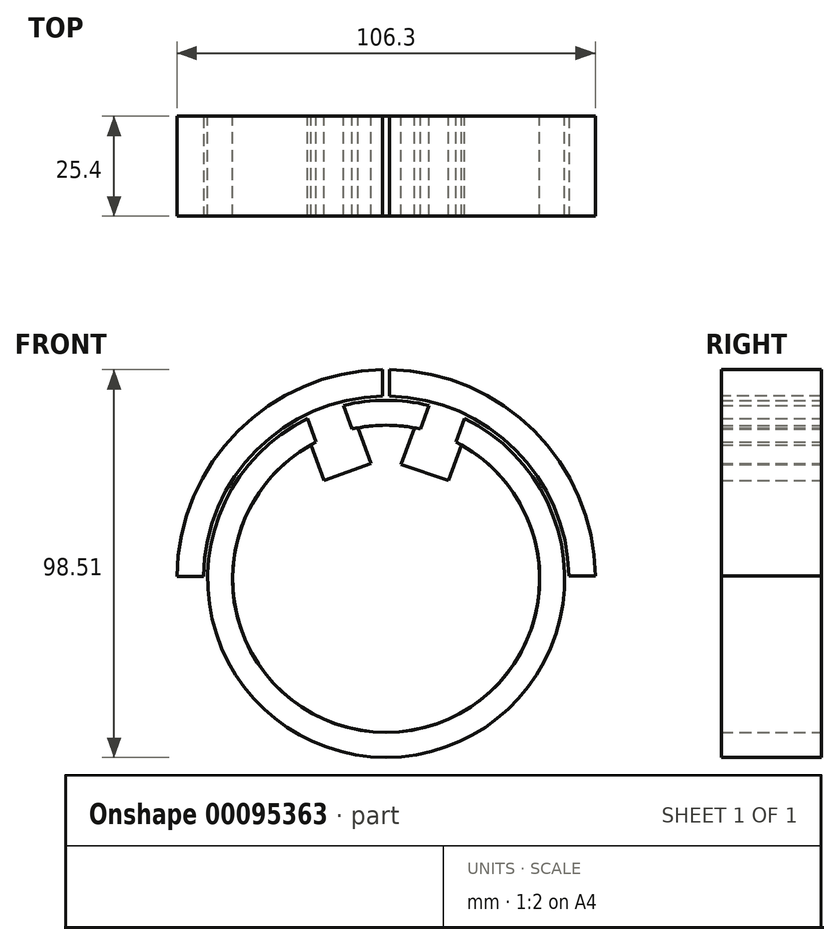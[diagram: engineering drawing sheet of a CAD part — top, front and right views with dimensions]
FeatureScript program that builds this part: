
annotation { "Feature Type Name" : "Feature", "Feature Type Description" : "" }
export const myFeature = defineFeature(function(context is Context, id is Id, definition is map)
    precondition{}
    {
        {
            var Q0;
            Q0=qCreatedBy(makeId("Front.planeOp"),FACE);
            var sketch = newSketch(context, id + "F0", { "sketchPlane" : qUnion([Q0])});
            skArc(sketch, "E0", {"start": v(-19.96, 40.74) * mm, "mid": v(0, -45.36) * mm, "end": v(19.96, 40.74) * mm});
            skArc(sketch, "E1", {"start": v(-17.78, 34.73) * mm, "mid": v(0, -39.02) * mm, "end": v(17.78, 34.73) * mm});
            skLineSegment(sketch, "E2", {"start": v(0, 77.3) * mm, "end": v(0, -77.42) * mm, "construction": true});
            skLineSegment(sketch, "E3", {"start": v(-103.05, 0) * mm, "end": v(124.24, 0) * mm, "construction": true});
            skLineSegment(sketch, "E4", {"start": v(0, 0) * mm, "end": v(-22.26, 61.17) * mm, "construction": true});
            skLineSegment(sketch, "E5", {"start": v(0, 0) * mm, "end": v(-64.24, 23.38) * mm, "construction": true});
            skLineSegment(sketch, "E6", {"start": v(-19.13, 34) * mm, "end": v(-15.83, 24.93) * mm});
            skLineSegment(sketch, "E7", {"start": v(-15.83, 24.93) * mm, "end": v(-3.9, 29.28) * mm});
            skLineSegment(sketch, "E8", {"start": v(-3.9, 29.28) * mm, "end": v(-7.2, 38.35) * mm});
            skLineSegment(sketch, "E9", {"start": v(0, 0) * mm, "end": v(24.43, 67.1) * mm, "construction": true});
            skLineSegment(sketch, "E10", {"start": v(17.7, 34.52) * mm, "end": v(19.13, 34) * mm});
            skLineSegment(sketch, "E11", {"start": v(7.2, 38.35) * mm, "end": v(3.84, 29.1) * mm});
            skLineSegment(sketch, "E12", {"start": v(3.84, 29.1) * mm, "end": v(15.83, 24.93) * mm});
            skLineSegment(sketch, "E13", {"start": v(15.83, 24.93) * mm, "end": v(19.13, 34) * mm});
            skLineSegment(sketch, "E14", {"start": v(-17.78, 34.73) * mm, "end": v(-19.96, 40.74) * mm});
            skLineSegment(sketch, "E15", {"start": v(-8.7, 38.03) * mm, "end": v(-10.9, 44.04) * mm});
            skLineSegment(sketch, "E16", {"start": v(8.7, 38.03) * mm, "end": v(10.9, 44.04) * mm});
            skLineSegment(sketch, "E17", {"start": v(17.7, 34.52) * mm, "end": v(19.96, 40.74) * mm});
            skArc(sketch, "E18.trimOffspring", {"start": v(10.9, 44.04) * mm, "mid": v(0, 45.36) * mm, "end": v(-10.9, 44.04) * mm});
            skArc(sketch, "E19.trimOffspring", {"start": v(8.7, 38.03) * mm, "mid": v(0, 39.02) * mm, "end": v(-8.7, 38.03) * mm});
            skSolve(sketch);
        }
        {
            var Q0;
            {var subQ3=sQuery(id+"F0.wireOp",EDGE,"E15");Q0=makeQuery(id+"F0.imprint","IMPRINT",FACE,{"disambiguationData":[TD([[makeQuery(id+"F0.imprint","IMPRINT",EDGE,{"derivedFrom":subQ3}),-1.0]])]});}
            var Q1;
            {var subQ6=sQuery(id+"F0.wireOp",EDGE,"E0");Q1=makeQuery(id+"F0.imprint","IMPRINT",FACE,{"disambiguationData":[TD([[makeQuery(id+"F0.imprint","IMPRINT",EDGE,{"derivedFrom":subQ6}),1.0]])]});}
            extrude(context, id + "F1", {"entities" : qUnion([Q0, Q1]), "depth" : 25.4 * mm});
        }
        {
            var Q0;
            {var subQ1=sQuery(id+"F0.wireOp",EDGE,"E6");Q0=makeQuery(id+"F0.imprint","IMPRINT",FACE,{"disambiguationData":[TD([[makeQuery(id+"F0.imprint","IMPRINT",EDGE,{"derivedFrom":subQ1}),-1.0]])]});}
            var sketch = newSketch(context, id + "F2", { "sketchPlane" : qUnion([Q0])});
            skSolve(sketch);
        }
        {
            var Q0;
            {var subQ1=sQuery(id+"F0.wireOp",EDGE,"E6");Q0=makeQuery(id+"F2.imprint","IMPRINT",FACE,{"disambiguationData":[TD([[makeQuery(id+"F2.imprint","IMPRINT",EDGE,{"derivedFrom":makeQuery(id+"F0.imprint","IMPRINT",EDGE,{"derivedFrom":subQ1})}),-1.0]])]});}
            extrude(context, id + "F3", {"entities" : qUnion([Q0]), "depth" : 25.4 * mm});
        }
        {
            var Q0;
            Q0=makeQuery(id+"F3.opExtrude","CAP_FACE",FACE,{"disambiguationData":[OSD([sQuery(id+"F0.wireOp",EDGE,"E1"),sQuery(id+"F0.wireOp",EDGE,"E6"),sQuery(id+"F0.wireOp",EDGE,"E7"),sQuery(id+"F0.wireOp",EDGE,"E8"),sQuery(id+"F0.wireOp",EDGE,"E11"),sQuery(id+"F0.wireOp",EDGE,"E12"),sQuery(id+"F0.wireOp",EDGE,"E13"),sQuery(id+"F0.wireOp",EDGE,"E19.trimOffspring")])],"isStart":false});
            var sketch = newSketch(context, id + "F4", { "sketchPlane" : qUnion([Q0])});
            skArc(sketch, "E20", {"start": v(-0.88, 46.41) * mm, "mid": v(-32.9, 32.75) * mm, "end": v(-46.42, 0.66) * mm});
            skArc(sketch, "E21", {"start": v(-0.88, 53.15) * mm, "mid": v(-37.67, 37.51) * mm, "end": v(-53.15, 0.66) * mm});
            skLineSegment(sketch, "E22", {"start": v(-0.88, 53.15) * mm, "end": v(-0.88, 46.41) * mm});
            skLineSegment(sketch, "E23", {"start": v(0.86, 53.15) * mm, "end": v(0.86, 46.41) * mm});
            skLineSegment(sketch, "E24", {"start": v(-53.15, 0.66) * mm, "end": v(-46.42, 0.66) * mm});
            skLineSegment(sketch, "E25", {"start": v(-53.15, -0.69) * mm, "end": v(-46.41, -0.69) * mm});
            skArc(sketch, "E26.trimOffspring", {"start": v(-53.15, -0.69) * mm, "mid": v(-0.07, -53.16) * mm, "end": v(53.15, -0.83) * mm});
            skArc(sketch, "E27.trimOffspring", {"start": v(-46.41, -0.69) * mm, "mid": v(-0.07, -46.42) * mm, "end": v(46.41, -0.83) * mm});
            skLineSegment(sketch, "E28", {"start": v(46.37, 0.7) * mm, "end": v(53.15, 0.7) * mm});
            skLineSegment(sketch, "E29", {"start": v(46.41, -0.83) * mm, "end": v(53.15, -0.83) * mm});
            skArc(sketch, "E30.trimOffspring", {"start": v(46.41, 0.7) * mm, "mid": v(32.88, 32.77) * mm, "end": v(0.86, 46.41) * mm});
            skArc(sketch, "E31.trimOffspring", {"start": v(53.15, 0.7) * mm, "mid": v(37.64, 37.53) * mm, "end": v(0.86, 53.15) * mm});
            skSolve(sketch);
        }
        {
            var Q0;
            Q0=makeQuery(id+"F4.imprint","IMPRINT",FACE,{"disambiguationData":[TD([[makeQuery(id+"F4.imprint","IMPRINT",EDGE,{"derivedFrom":sQuery(id+"F4.wireOp",EDGE,"E20")}),-1.0]])]});
            extrude(context, id + "F5", {"entities" : qUnion([Q0]), "oppositeDirection" : true, "depth" : 25.4 * mm});
        }
        {
            var Q0;
            Q0=makeQuery(id+"F4.imprint","IMPRINT",FACE,{"disambiguationData":[TD([[makeQuery(id+"F4.imprint","IMPRINT",EDGE,{"derivedFrom":sQuery(id+"F4.wireOp",EDGE,"E23")}),1.0]])]});
            extrude(context, id + "F6", {"entities" : qUnion([Q0]), "oppositeDirection" : true, "depth" : 25.4 * mm});
        }
    });
